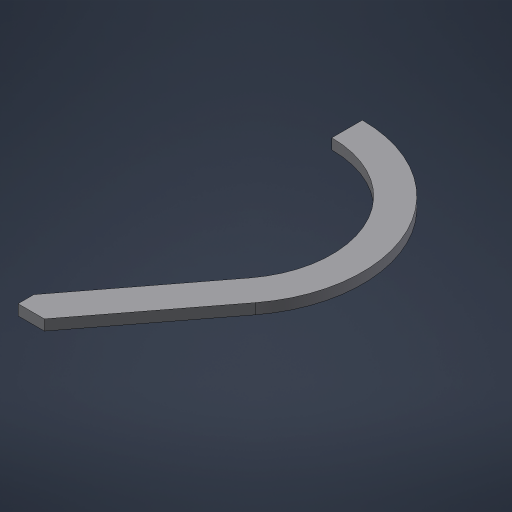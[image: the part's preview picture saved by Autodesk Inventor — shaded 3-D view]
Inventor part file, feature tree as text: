
AUTODESK INVENTOR PART (.ipt)
format: ipt  version: 2023.5 (Build 275446000, 446)  size: 376,320 bytes
history: native  units: mm
features: extrude x1, sketch x1
ambient origin geometry x8: Origin, YZ Plane, XZ Plane, XY Plane, X Axis, Y Axis, Z Axis, Center Point
bodies: Volumenkörper1 (feature_tree)
feature tree (2):
  extrude  "Extrusion1"  Depth=5.0mm
  sketch  "Skizze1"  dims[d0=3.0mm d1=5.0mm d2=25.0mm d3=60.0mm d4=2.0mm d5=0.0mm]
